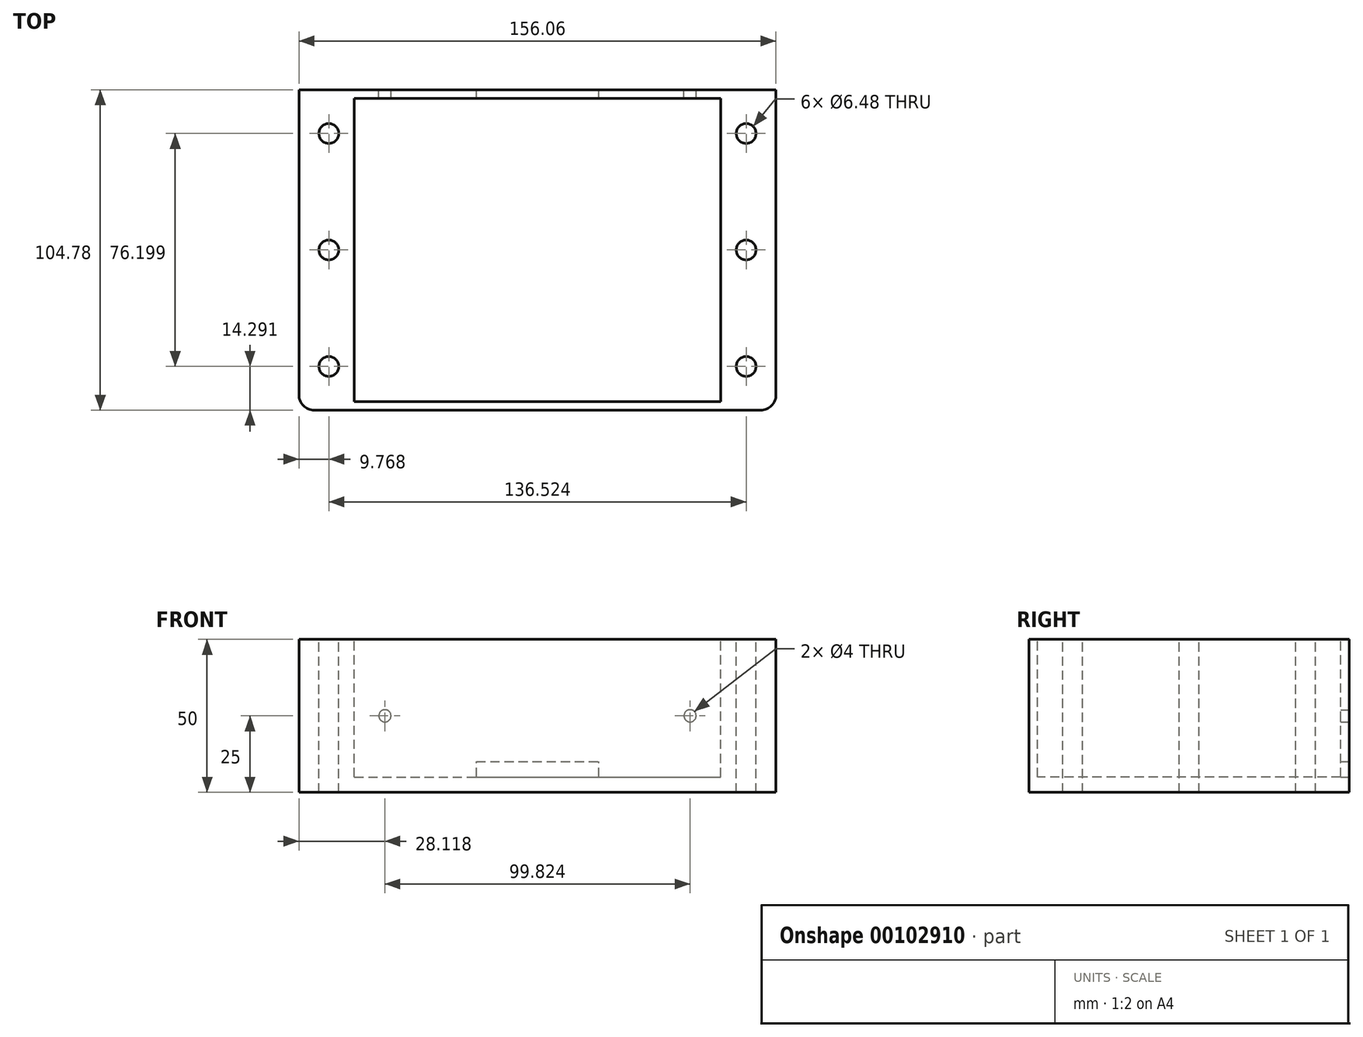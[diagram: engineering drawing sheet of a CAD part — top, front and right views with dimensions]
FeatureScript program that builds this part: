
annotation { "Feature Type Name" : "Feature", "Feature Type Description" : "" }
export const myFeature = defineFeature(function(context is Context, id is Id, definition is map)
    precondition{}
    {
        {
            var Q0;
            Q0=qCreatedBy(makeId("Top.planeOp"),FACE);
            var sketch = newSketch(context, id + "F0", { "sketchPlane" : qUnion([Q0])});
            skLineSegment(sketch, "E0", {"start": v(68.26, 31.75) * mm, "end": v(72.22, 31.75) * mm});
            skLineSegment(sketch, "E1", {"start": v(72.22, 6.35) * mm, "end": v(72.22, 31.75) * mm});
            skLineSegment(sketch, "E2", {"start": v(68.26, 6.35) * mm, "end": v(72.22, 6.35) * mm});
            skArc(sketch, "E3", {"start": v(68.26, 6.35) * mm, "mid": v(61.91, 0) * mm, "end": v(68.26, -6.35) * mm});
            skLineSegment(sketch, "E4", {"start": v(68.26, -6.35) * mm, "end": v(72.22, -6.35) * mm});
            skLineSegment(sketch, "E5", {"start": v(72.22, -31.75) * mm, "end": v(72.22, -6.35) * mm});
            skLineSegment(sketch, "E6", {"start": v(68.26, -31.75) * mm, "end": v(72.22, -31.75) * mm});
            skArc(sketch, "E7", {"start": v(68.26, -31.75) * mm, "mid": v(61.91, -38.1) * mm, "end": v(68.26, -44.45) * mm});
            skLineSegment(sketch, "E8", {"start": v(68.26, -44.45) * mm, "end": v(72.22, -44.45) * mm});
            skLineSegment(sketch, "E9", {"start": v(72.22, -51.59) * mm, "end": v(72.22, -44.45) * mm});
            skLineSegment(sketch, "E10", {"start": v(-72.23, -51.59) * mm, "end": v(72.23, -51.59) * mm});
            skLineSegment(sketch, "E11", {"start": v(-72.23, -51.59) * mm, "end": v(-72.23, -44.45) * mm});
            skLineSegment(sketch, "E12", {"start": v(-68.26, -44.45) * mm, "end": v(-72.23, -44.45) * mm});
            skArc(sketch, "E13", {"start": v(-68.26, -44.45) * mm, "mid": v(-61.91, -38.1) * mm, "end": v(-68.26, -31.75) * mm});
            skLineSegment(sketch, "E14", {"start": v(-68.26, -31.75) * mm, "end": v(-72.23, -31.75) * mm});
            skLineSegment(sketch, "E15", {"start": v(-72.23, -31.75) * mm, "end": v(-72.23, -6.35) * mm});
            skLineSegment(sketch, "E16", {"start": v(-68.26, -6.35) * mm, "end": v(-72.23, -6.35) * mm});
            skArc(sketch, "E17", {"start": v(-68.26, -6.35) * mm, "mid": v(-61.91, 0) * mm, "end": v(-68.26, 6.35) * mm});
            skLineSegment(sketch, "E18", {"start": v(-68.26, 6.35) * mm, "end": v(-72.23, 6.35) * mm});
            skLineSegment(sketch, "E19", {"start": v(-72.23, 6.35) * mm, "end": v(-72.23, 31.75) * mm});
            skLineSegment(sketch, "E20", {"start": v(-68.26, 31.75) * mm, "end": v(-72.23, 31.75) * mm});
            skArc(sketch, "E21", {"start": v(-68.26, 31.75) * mm, "mid": v(-61.91, 38.1) * mm, "end": v(-68.26, 44.45) * mm});
            skLineSegment(sketch, "E22", {"start": v(-68.26, 44.45) * mm, "end": v(-72.23, 44.45) * mm});
            skLineSegment(sketch, "E23", {"start": v(-72.23, 44.45) * mm, "end": v(-72.23, 51.59) * mm});
            skLineSegment(sketch, "E24", {"start": v(72.22, 51.59) * mm, "end": v(-72.23, 51.59) * mm});
            skLineSegment(sketch, "E25", {"start": v(72.22, 44.45) * mm, "end": v(72.22, 51.59) * mm});
            skLineSegment(sketch, "E26", {"start": v(68.26, 44.45) * mm, "end": v(72.22, 44.45) * mm});
            skArc(sketch, "E27", {"start": v(68.26, 44.45) * mm, "mid": v(61.91, 38.1) * mm, "end": v(68.26, 31.75) * mm});
            skCircle(sketch, "E28", {"center": v(-68.26, 0) * mm, "radius": 3.24 * mm});
            skCircle(sketch, "E29", {"center": v(-68.26, -38.1) * mm, "radius": 3.24 * mm});
            skCircle(sketch, "E30", {"center": v(68.26, 0) * mm, "radius": 3.24 * mm});
            skCircle(sketch, "E31", {"center": v(-68.26, 38.1) * mm, "radius": 3.24 * mm});
            skCircle(sketch, "E32", {"center": v(68.26, -38.1) * mm, "radius": 3.24 * mm});
            skCircle(sketch, "E33", {"center": v(68.26, 38.1) * mm, "radius": 3.24 * mm});
            skLineSegment(sketch, "E34", {"start": v(-73.03, -52.39) * mm, "end": v(-73.03, 52.39) * mm});
            skLineSegment(sketch, "E35", {"start": v(73.03, -52.39) * mm, "end": v(73.03, 52.39) * mm});
            skLineSegment(sketch, "E36", {"start": v(73.03, 52.39) * mm, "end": v(-73.03, 52.39) * mm});
            skLineSegment(sketch, "E37", {"start": v(-73.03, -52.39) * mm, "end": v(73.03, -52.39) * mm});
            skLineSegment(sketch, "E38.bottom", {"start": v(73.03, 52.39) * mm, "end": v(78.03, 52.39) * mm});
            skLineSegment(sketch, "E38.top", {"start": v(73.03, -52.39) * mm, "end": v(78.03, -52.39) * mm});
            skLineSegment(sketch, "E38.left", {"start": v(73.03, 52.39) * mm, "end": v(73.03, -52.39) * mm});
            skLineSegment(sketch, "E38.right", {"start": v(78.03, 52.39) * mm, "end": v(78.03, -52.39) * mm});
            skLineSegment(sketch, "E39.MirrorCS", {"start": v(-73.03, -52.39) * mm, "end": v(-78.03, -52.39) * mm});
            skLineSegment(sketch, "E40.MirrorCS", {"start": v(-78.03, 52.39) * mm, "end": v(-78.03, -52.39) * mm});
            skLineSegment(sketch, "E41.MirrorCS", {"start": v(-73.03, 52.39) * mm, "end": v(-78.03, 52.39) * mm});
            skSolve(sketch);
        }
        {
            var Q0;
            Q0 = qSketchRegion(id + "F0", true);
            var Q1;
            Q1=makeQuery(id+"F0.imprint","IMPRINT",FACE,{"disambiguationData":[TD([[makeQuery(id+"F0.imprint","IMPRINT",EDGE,{"derivedFrom":sQuery(id+"F0.wireOp",EDGE,"E31")}),-1.0]])]});
            var Q2;
            Q2=makeQuery(id+"F0.imprint","IMPRINT",FACE,{"disambiguationData":[TD([[makeQuery(id+"F0.imprint","IMPRINT",EDGE,{"derivedFrom":sQuery(id+"F0.wireOp",EDGE,"E6")}),1.0]])]});
            var Q3;
            Q3=makeQuery(id+"F0.imprint","IMPRINT",FACE,{"disambiguationData":[TD([[makeQuery(id+"F0.imprint","IMPRINT",EDGE,{"derivedFrom":sQuery(id+"F0.wireOp",EDGE,"E28")}),-1.0]])]});
            var Q4;
            Q4=makeQuery(id+"F0.imprint","IMPRINT",FACE,{"disambiguationData":[TD([[makeQuery(id+"F0.imprint","IMPRINT",EDGE,{"derivedFrom":sQuery(id+"F0.wireOp",EDGE,"E29")}),-1.0]])]});
            var Q5;
            Q5=makeQuery(id+"F0.imprint","IMPRINT",FACE,{"disambiguationData":[TD([[makeQuery(id+"F0.imprint","IMPRINT",EDGE,{"derivedFrom":sQuery(id+"F0.wireOp",EDGE,"E32")}),-1.0]])]});
            var Q6;
            Q6=makeQuery(id+"F0.imprint","IMPRINT",FACE,{"disambiguationData":[TD([[makeQuery(id+"F0.imprint","IMPRINT",EDGE,{"derivedFrom":sQuery(id+"F0.wireOp",EDGE,"E30")}),-1.0]])]});
            var Q7;
            Q7=makeQuery(id+"F0.imprint","IMPRINT",FACE,{"disambiguationData":[TD([[makeQuery(id+"F0.imprint","IMPRINT",EDGE,{"derivedFrom":sQuery(id+"F0.wireOp",EDGE,"E33")}),-1.0]])]});
            extrude(context, id + "F1", {"entities" : qUnion([Q0, Q1, Q2, Q3, Q4, Q5, Q6, Q7]), "oppositeDirection" : true, "depth" : 50 * mm});
        }
        {
            var Q0;
            Q0=makeQuery(id+"F0.imprint","IMPRINT",FACE,{"disambiguationData":[TD([[makeQuery(id+"F0.imprint","IMPRINT",EDGE,{"derivedFrom":sQuery(id+"F0.wireOp",EDGE,"E6")}),1.0]])]});
            var sketch = newSketch(context, id + "F2", { "sketchPlane" : qUnion([Q0])});
            skLineSegment(sketch, "E42.bottom", {"start": v(-59.91, 49.59) * mm, "end": v(59.91, 49.59) * mm});
            skLineSegment(sketch, "E42.top", {"start": v(-59.91, -49.59) * mm, "end": v(59.91, -49.59) * mm});
            skLineSegment(sketch, "E42.left", {"start": v(-59.91, 49.59) * mm, "end": v(-59.91, -49.59) * mm});
            skLineSegment(sketch, "E42.right", {"start": v(59.91, 49.59) * mm, "end": v(59.91, -49.59) * mm});
            skPoint(sketch, "E42.middle", {"position": v(0, 0) * mm});
            skSolve(sketch);
        }
        {
            var Q0;
            Q0 = qSketchRegion(id + "F2", true);
            extrude(context, id + "F3", {"entities" : qUnion([Q0]), "operationType" : NewBodyOperationType.REMOVE, "oppositeDirection" : true, "depth" : 45 * mm});
        }
        {
            var Q0;
            Q0=sQuery(id+"F0.wireOp",VERTEX,"E21.center");
            var Q1;
            Q1=sQuery(id+"F0.wireOp",VERTEX,"E17.center");
            var Q2;
            Q2=sQuery(id+"F0.wireOp",VERTEX,"E13.center");
            var Q3;
            Q3=sQuery(id+"F0.wireOp",VERTEX,"E7.center");
            var Q4;
            Q4=sQuery(id+"F0.wireOp",VERTEX,"E27.center");
            var Q5;
            Q5=sQuery(id+"F0.wireOp",VERTEX,"E3.center");
            var Q6;
            Q6=makeQuery(id+"F1.opExtrude","SWEPT_BODY",BODY,{"disambiguationData":[OSD([sQuery(id+"F0.wireOp",EDGE,"E36"),sQuery(id+"F0.wireOp",EDGE,"E37"),sQuery(id+"F0.wireOp",EDGE,"E38.bottom"),sQuery(id+"F0.wireOp",EDGE,"E38.top"),sQuery(id+"F0.wireOp",EDGE,"E38.right"),sQuery(id+"F0.wireOp",EDGE,"E39.MirrorCS"),sQuery(id+"F0.wireOp",EDGE,"E40.MirrorCS"),sQuery(id+"F0.wireOp",EDGE,"E41.MirrorCS")])]});
            hole(context, id + "F4", {"style" : HoleStyle.SIMPLE, "endStyle" : HoleEndStyle.BLIND, "holeDiameter" : 5.6 * mm, "holeDepth" : 20 * mm, "locations" : qUnion([Q0, Q1, Q2, Q3, Q4, Q5]), "scope" : qUnion([Q6])});
        }
        {
            var Q0;
            Q0=makeQuery(id+"F1.opExtrude","SWEPT_FACE",FACE,{"disambiguationData":[OSD([sQuery(id+"F0.wireOp",EDGE,"E36"),sQuery(id+"F0.wireOp",EDGE,"E38.bottom"),sQuery(id+"F0.wireOp",EDGE,"E41.MirrorCS")])]});
            var sketch = newSketch(context, id + "F5", { "sketchPlane" : qUnion([Q0])});
            skLineSegment(sketch, "E43.bottom", {"start": v(20, -45) * mm, "end": v(-20, -45) * mm});
            skLineSegment(sketch, "E43.top", {"start": v(20, -40) * mm, "end": v(-20, -40) * mm});
            skLineSegment(sketch, "E43.left", {"start": v(20, -45) * mm, "end": v(20, -40) * mm});
            skLineSegment(sketch, "E43.right", {"start": v(-20, -45) * mm, "end": v(-20, -40) * mm});
            skPoint(sketch, "E43.middle", {"position": v(0, -42.5) * mm});
            skPoint(sketch, "E44", {"position": v(-49.91, -25) * mm});
            skPoint(sketch, "E44.positionSnap0", {"position": v(-78.03, -25) * mm});
            skPoint(sketch, "E45.MirrorP", {"position": v(49.91, -25) * mm});
            skSolve(sketch);
        }
        {
            var Q0;
            Q0=makeQuery(id+"F5.imprint","IMPRINT",FACE,{"disambiguationData":[TD([[makeQuery(id+"F5.imprint","IMPRINT",EDGE,{"derivedFrom":sQuery(id+"F5.wireOp",EDGE,"E43.bottom")}),-1.0]])]});
            extrude(context, id + "F6", {"entities" : qUnion([Q0]), "operationType" : NewBodyOperationType.REMOVE, "endBound" : BoundingType.UP_TO_NEXT, "oppositeDirection" : true, "depth" : 25 * mm});
        }
        {
            var Q0;
            Q0=sQuery(id+"F5.wireOp",VERTEX,"E44");
            var Q1;
            Q1=sQuery(id+"F5.wireOp",VERTEX,"E45.MirrorP");
            var Q2;
            Q2=makeQuery(id+"F1.opExtrude","SWEPT_BODY",BODY,{"disambiguationData":[OSD([sQuery(id+"F0.wireOp",EDGE,"E36"),sQuery(id+"F0.wireOp",EDGE,"E37"),sQuery(id+"F0.wireOp",EDGE,"E38.bottom"),sQuery(id+"F0.wireOp",EDGE,"E38.top"),sQuery(id+"F0.wireOp",EDGE,"E38.right"),sQuery(id+"F0.wireOp",EDGE,"E39.MirrorCS"),sQuery(id+"F0.wireOp",EDGE,"E40.MirrorCS"),sQuery(id+"F0.wireOp",EDGE,"E41.MirrorCS")])]});
            hole(context, id + "F7", {"style" : HoleStyle.SIMPLE, "endStyle" : HoleEndStyle.BLIND, "holeDiameter" : 4 * mm, "holeDepth" : 20 * mm, "locations" : qUnion([Q0, Q1]), "scope" : qUnion([Q2])});
        }
        {
            var Q0;
            Q0=makeQuery(id+"F1.opExtrude","SWEPT_EDGE",EDGE,{"disambiguationData":[OSD([sQuery(id+"F0.wireOp",EDGE,"E39.MirrorCS"),sQuery(id+"F0.wireOp",EDGE,"E40.MirrorCS")])]});
            var Q1;
            Q1=makeQuery(id+"F1.opExtrude","SWEPT_EDGE",EDGE,{"disambiguationData":[OSD([sQuery(id+"F0.wireOp",EDGE,"E38.top"),sQuery(id+"F0.wireOp",EDGE,"E38.right")])]});
            fillet(context, id + "F8", {"entities" : qUnion([Q0, Q1]), "radius" : 5 * mm, "tangentPropagation" : true, "allowEdgeOverflow" : false});
        }
    });
